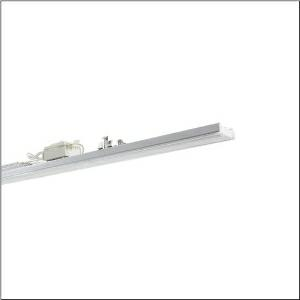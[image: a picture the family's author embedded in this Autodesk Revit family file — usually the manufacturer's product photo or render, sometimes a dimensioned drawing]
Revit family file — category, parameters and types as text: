
# Revit family: licross_r__21_recessed_mo_52tl11dn68xg3s_a87a
name_source: partatom
category: Lighting Fixtures
units: mm (PartAtom-declared; Revit-internal decimal feet)

## family parameters
Cut with Voids When Loaded = No
Host = Face
Light Source = No
Part Type = Normal
Room Calculation Point = No
Round Connector Dimension = Use Diameter
Shared = No

## types (1)
- --- (1 x LED, 910 lm, 6.7 W, 6500K)
    Apparent Load = 7 VA
    CIE Flux Codes = 89 96 99 100 100
    Color Rendering = 80
    Color Temperature = 6500K
    Default Elevation = 1800 mm
    Description = Licross® 21 Recessed MO, luminaire insert, of sheet steel, galvanised, coil coated, white, length: 1.500mm, width: 66mm, height: 67mm, LED rated luminous flux: 8.000lm, light colour: 865, control gear: DALI 2 (for two DALI lines), with plug, 6-pole, with phase selection, for trunking rail, 14-core, mains connection: 220..240V, AC, 50/60Hz, rated input power: 46W, for emergency light function, internal wiring halogen-free, for trunking rail, 14-core, converter,control gear: single battery element, battery: LiFePO4, 9Ah, primary optical cover: cover, of PMMA, light emission: direct distribution, primary light characteristic: symmetric, protection rating (complete): IP40, insulation class (complete): insulation class I (protective earthing), certification: CE, UKCA, protection symbol: D if used in an environment without relevant dust loads with corresponding accessories, impact resistance: IK06, permissible ambient temperature for indoor applications: +5..+35°C, standard: EN 60598-2-22, corresponds to IFS (International Featured Standards) requirements for safety and quality in the food industry, reducing of maximum allowable ambient temperature of 5°C with ceiling mounting, LABS conformity tested according to VDMA 24364:2018-05, packaging unit: 1 piece
    Height = 58 mm
    Lamp = 1 x LED
    Lamp Light Flux = 910 lm
    Lamp Power = 6.7 W
    Lamp count = 1
    Length = 1500 mm
    Luminous efficacy = 136 lm/W
    Manufacturer = Siteco
    ModVariant = No
    Model = 52TL11DN68XG3S
    Mounting Place = Ceiling
    Mounting Type = Pendant
    Number of Poles = 1
    OnlyDefault = Yes
    Power Factor = 1
    Product Name = Licross® 21 Recessed MO
    Product group = luminaire insert | ceiling pendant
    ProductGroupID = 902
    Protection Class = Protection class I
    Protection Degree = IP 40
    RLX_Detail_Level = 1
    RLX_Emergency_Light_Flux = 0 lm
    RLX_Emergency_Type = 0
    RLX_Emergency_Type_DB = No
    RlxData = <blob elided: 24933 chars, md5=61a3e2f7>
    Socket = socket
    Standby Power = 0 W
    System Light Flux = 910 lm
    System Power = 7 W
    Type Comments = : emergency light operation: 3 h
    Type Image = l_1296930.jpg
    URL = http://relux.com
    VarID = @adj_030193
    Voltage = 0 V
    Weight = 0.00 kg
    Width = 66 mm

## geometry (parser evidence)
native form markers: Blend x4, Sweep x11
no freeform markers — native parametric forms only
